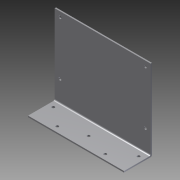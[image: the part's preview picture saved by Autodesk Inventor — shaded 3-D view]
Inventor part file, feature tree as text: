
AUTODESK INVENTOR PART (.ipt)
format: ipt  version: 2012 (Build 160160000, 160)  size: 134,144 bytes
history: native  units: in
note: dims shown in document units (in); Inventor stores cm internally (conversion verified against a paired STEP export)
features: extrude x4, sketch x4, fillet x1
ambient origin geometry x8: Origin, YZ Plane, XZ Plane, XY Plane, X Axis, Y Axis, Z Axis, Center Point
bodies: Solid1 (feature_tree)
feature tree (9):
  extrude  "Extrusion1"  Depth=7.6in
  extrude  "Extrusion2"  Depth=9.0in
  fillet  "Fillet1"  Radius=0.125in
  extrude  "Extrusion3"  Depth=0.125in
  extrude  "Extrusion4"  Depth=0.25in
  sketch  "Sketch1"  dims[d0=9.0in d1=7.6in]
  sketch  "Sketch2"  dims[d2=0.125in d3=0.0in d4=9.0in d5=0.125in]
  sketch  "Sketch3"  dims[d6=2.5in d7=0.0in d8=0.125in]
  sketch  "Sketch4"  dims[d9=0.25in d10=0.25in d11=0.25in d12=0.25in d13=0.25in d14=0.5in d15=0.5in d16=0.5in d17=0.5in d18=4.5in d19=9.0in d20=2.25in d21=0.5in d22=0.5in d23=2.25in d24=1.1875in d25=2.375in d26=2.5in d27=0.0in d28=0.25in d29=0.25in d30=0.5in d31=0.5in d32=0.5in d33=0.5in d34=0.25in d35=0.25in d36=0.5in d37=0.5in d38=5.0in d39=5.0in d40=2.5in d41=0.0in]
